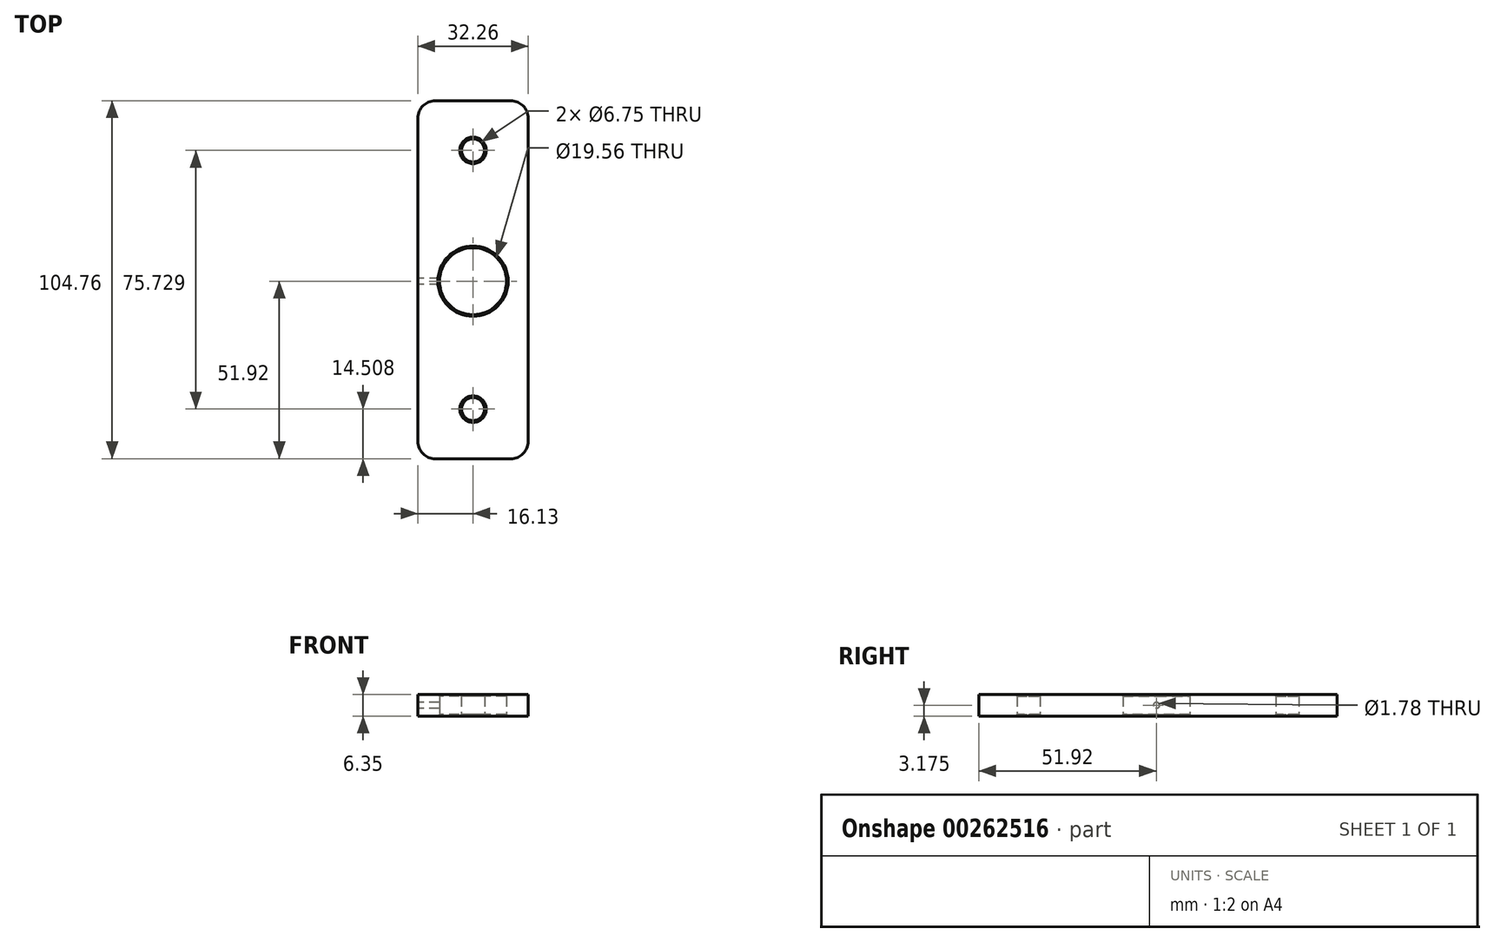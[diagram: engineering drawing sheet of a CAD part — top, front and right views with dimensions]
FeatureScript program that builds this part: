
annotation { "Feature Type Name" : "Feature", "Feature Type Description" : "" }
export const myFeature = defineFeature(function(context is Context, id is Id, definition is map)
    precondition{}
    {
        {
            var Q0;
            Q0=qCreatedBy(makeId("Top.planeOp"),FACE);
            var sketch = newSketch(context, id + "F0", { "sketchPlane" : qUnion([Q0])});
            skLineSegment(sketch, "E0.bottom", {"start": v(-16.13, -51.92) * mm, "end": v(16.13, -51.92) * mm});
            skLineSegment(sketch, "E0.top", {"start": v(-16.13, 52.84) * mm, "end": v(16.13, 52.84) * mm});
            skLineSegment(sketch, "E0.left", {"start": v(-16.13, -51.92) * mm, "end": v(-16.13, 52.84) * mm});
            skLineSegment(sketch, "E0.right", {"start": v(16.13, -51.92) * mm, "end": v(16.13, 52.84) * mm});
            skCircle(sketch, "E1", {"center": v(0, 0) * mm, "radius": 9.78 * mm});
            skCircle(sketch, "E2", {"center": v(0, 38.32) * mm, "radius": 3.37 * mm});
            skCircle(sketch, "E3", {"center": v(0, -37.41) * mm, "radius": 3.37 * mm});
            skSolve(sketch);
        }
        {
            var Q0;
            Q0=makeQuery(id+"F0.imprint","IMPRINT",FACE,{"disambiguationData":[TD([[makeQuery(id+"F0.imprint","IMPRINT",EDGE,{"derivedFrom":sQuery(id+"F0.wireOp",EDGE,"E0.bottom")}),1.0]])]});
            extrude(context, id + "F1", {"entities" : qUnion([Q0]), "depth" : 6.35 * mm});
        }
        {
            var Q0;
            Q0=makeQuery(id+"F1.opExtrude","SWEPT_FACE",FACE,{"disambiguationData":[OSD([sQuery(id+"F0.wireOp",EDGE,"E0.left")])]});
            var sketch = newSketch(context, id + "F2", { "sketchPlane" : qUnion([Q0])});
            skCircle(sketch, "E4", {"center": v(0, 3.18) * mm, "radius": 0.89 * mm});
            skLineSegment(sketch, "E5", {"start": v(0, 6.35) * mm, "end": v(0, 3.18) * mm, "construction": true});
            skLineSegment(sketch, "E6", {"start": v(0, 3.18) * mm, "end": v(0, 0) * mm, "construction": true});
            skSolve(sketch);
        }
        {
            var Q0;
            Q0 = qSketchRegion(id + "F2", true);
            extrude(context, id + "F3", {"entities" : qUnion([Q0]), "operationType" : NewBodyOperationType.REMOVE, "endBound" : BoundingType.UP_TO_NEXT, "oppositeDirection" : true, "depth" : 25.4 * mm});
        }
        {
            var Q0;
            Q0=makeQuery(id+"F1.opExtrude","SWEPT_EDGE",EDGE,{"disambiguationData":[OSD([sQuery(id+"F0.wireOp",EDGE,"E0.top"),sQuery(id+"F0.wireOp",EDGE,"E0.left")])]});
            var Q1;
            Q1=makeQuery(id+"F1.opExtrude","SWEPT_EDGE",EDGE,{"disambiguationData":[OSD([sQuery(id+"F0.wireOp",EDGE,"E0.bottom"),sQuery(id+"F0.wireOp",EDGE,"E0.left")])]});
            var Q2;
            Q2=makeQuery(id+"F1.opExtrude","SWEPT_EDGE",EDGE,{"disambiguationData":[OSD([sQuery(id+"F0.wireOp",EDGE,"E0.bottom"),sQuery(id+"F0.wireOp",EDGE,"E0.right")])]});
            var Q3;
            Q3=makeQuery(id+"F1.opExtrude","SWEPT_EDGE",EDGE,{"disambiguationData":[OSD([sQuery(id+"F0.wireOp",EDGE,"E0.top"),sQuery(id+"F0.wireOp",EDGE,"E0.right")])]});
            fillet(context, id + "F4", {"entities" : qUnion([Q0, Q1, Q2, Q3]), "radius" : 5.08 * mm, "tangentPropagation" : true, "allowEdgeOverflow" : false});
        }
        {
            var Q0;
            Q0=makeQuery(id+"F1.opExtrude","CAP_EDGE",EDGE,{"disambiguationData":[OSD([sQuery(id+"F0.wireOp",EDGE,"E2")])],"isStart":false});
            var Q1;
            Q1=makeQuery(id+"F1.opExtrude","CAP_EDGE",EDGE,{"disambiguationData":[OSD([sQuery(id+"F0.wireOp",EDGE,"E2")])],"isStart":true});
            var Q2;
            Q2=makeQuery(id+"F1.opExtrude","CAP_EDGE",EDGE,{"disambiguationData":[OSD([sQuery(id+"F0.wireOp",EDGE,"E1")])],"isStart":true});
            var Q3;
            Q3=makeQuery(id+"F1.opExtrude","CAP_EDGE",EDGE,{"disambiguationData":[OSD([sQuery(id+"F0.wireOp",EDGE,"E3")])],"isStart":true});
            var Q4;
            Q4=makeQuery(id+"F1.opExtrude","CAP_EDGE",EDGE,{"disambiguationData":[OSD([sQuery(id+"F0.wireOp",EDGE,"E3")])],"isStart":false});
            var Q5;
            Q5=makeQuery(id+"F1.opExtrude","CAP_EDGE",EDGE,{"disambiguationData":[OSD([sQuery(id+"F0.wireOp",EDGE,"E1")])],"isStart":false});
            chamfer(context, id + "F5", {"entities" : qUnion([Q0, Q1, Q2, Q3, Q4, Q5]), "width" : 0.5 * mm, "tangentPropagation" : true});
        }
    });
